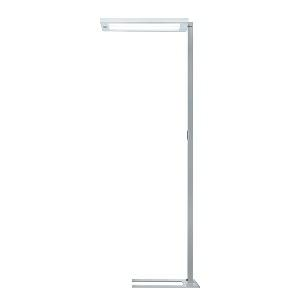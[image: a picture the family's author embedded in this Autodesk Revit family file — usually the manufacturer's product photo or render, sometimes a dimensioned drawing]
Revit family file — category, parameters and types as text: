
# Revit family: lavigo_-_dps_16500_840_r_g2_00804524_fdbc
name_source: partatom
category: Lighting Fixtures
units: mm (PartAtom-declared; Revit-internal decimal feet)

## family parameters
Cut with Voids When Loaded = No
Host = Face
Light Source = No
Part Type = Normal
Room Calculation Point = No
Round Connector Dimension = Use Diameter
Shared = No

## types (1)
- LAVIGO - DPS 16500/840/R/G2 (1 x LED, 16150 lm, 4000K)
    Apparent Load = 113 VA
    Approval mark = CE
    CIE Flux Codes = 60 87 97 11 100
    Color Rendering = 80-89
    Color Temperature = 4000K
    Control Gear = Electronic ballast
    Default Elevation = 1800 mm
    Description = DPS 16500/840/R/G2|Free-standing luminaire|light source: LED|work equipment: Electronic ballast|connected load: 220-240 V, 50/60 Hz|Power consumption: approx. 113 W|standby: approx. 0,50|power factor: approx. 0,963|luminous flux: 16150 lm|luminous efficacy: 142 lm/W|light distribution: Direct/indirect|direct ratio: approx. 11 %|colour temperature: Cold white, ca. 4000 K|color rendering index (CRI): >= 80|chromaticity tolerance:  3 SDCM|technology: Presence and daylight sensor control (PIR)|operation: Multi-function switch|luminaire body|material: Steel/plastic|surface: Painted|colour: Silver metallic|lamp cover: Acrylic (PMMA), Satine|tubular section|material: Steel tube|surface: Painted|Form: Tubular section upright|colour of tubular section: Silver metallic|luminaire base|Form: C-form flat|weight (net): approx. 19.7 kg|mains lead: 3.00 m Mains plug CEE 7/VII|Fastening: Floor standing base|decorative contrast side parts: Flint grey|glare control: Prism aperture|luminance(L65): <= 3000 cd/m|unified glare rating(4H 8H): <=  16|special features: Luminaire head detachable, Cradle to Cradle Certified TM, Direct light component with edge light and light-guide technology for homogenous light exit, Flicker-free, Integrated light and presence sensor PIR, Retrofittable with TALK module, Separated, direct and indirect light individually adjustable|Approval mark: VDE - ENEC|
    Frequency = 50 Hz, 60 Hz
    Height = 36 mm
    Lamp = 1 x LED
    Lamp Light Flux = 16150 lm
    Lamp count = 1
    Length = 675 mm
    Luminous efficacy = 143 lm/W
    Manufacturer = Waldmann
    ModVariant = No
    Model = 00804524
    Mounting Place = Floor
    Mounting Type = Freestanding
    Number of Poles = 1
    OnlyDefault = Yes
    Power Factor = 1
    Product Name = LAVIGO - DPS 16500/840/R/G2
    Product group = Free standing luminaire
    ProductGroupID = 13
    Protection Class = Protection class I
    Protection Degree = IP 20
    RLX_Detail_Level = 1
    RLX_Emergency_Light_Flux = 0 lm
    RLX_Emergency_Type = 0
    RLX_Emergency_Type_DB = No
    RlxData = <blob elided: 37029 chars, md5=ff0ff1c2>
    Socket = socket
    Standby Power = 0 W
    System Light Flux = 16150 lm
    System Power = 113 W
    Type Comments = Product without accessories
    Type Image = 121695000-00625713.jpg
    URL = http://relux.com
    VarID = ---
    Voltage = 230 V
    Voltage Range = 220-240 V
    Weight = 0.00 kg
    Width = 320 mm

## geometry (parser evidence)
native form markers: Blend x4, Sweep x14
no freeform markers — native parametric forms only
